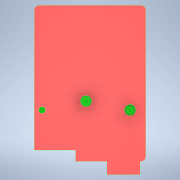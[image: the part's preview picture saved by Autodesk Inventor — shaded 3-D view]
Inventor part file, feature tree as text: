
AUTODESK INVENTOR PART (.ipt)
format: ipt  version: 2022 (Build 260153000, 153)  size: 168,448 bytes
history: native  units: mm
features: extrude x6, sketch x4, fillet x1
ambient origin geometry x8: Origin, YZ Plane, XZ Plane, XY Plane, X Axis, Y Axis, Z Axis, Center Point
bodies: Body1 (feature_tree)
feature tree (11):
  extrude  "Extrusion3"  Depth=70.0mm
  fillet  "Fillet1"  Radius=6.0mm
  sketch  "Sketch4"  dims[d14=2.0mm d16=18.5mm]
  extrude  "Extrusion5"  Depth=18.5mm
  extrude  "Extrusion6"  Depth=5.0mm
  extrude  "Extrusion7"  Depth=20.0mm TaperAngle=0.0deg
  extrude  "Extrusion8"  Depth=5.0mm
  extrude  "Extrusion9"  Depth=6.0mm
  sketch  "Sketch2"  dims[d0=50.0mm d1=70.0mm d12=6.0mm d13=0.0mm]
  sketch  "Sketch5"  dims[d17=5.0mm d31=5.0mm]
  sketch  "Sketch6"  dims[d34=3.0mm d37=20.0mm d38=0.0mm d41=5.0mm d44=19.75mm d45=19.75mm d46=7.0mm d48=5.6mm d49=0.0mm d50=3.0mm d51=14.5mm d52=0.0mm d53=10.64mm d54=0.0mm d55=3.0mm d56=9.36mm d57=0.0mm d58=2.5mm d59=15.0mm d60=6.0mm d61=23.0mm d62=27.0mm d63=23.0mm d4=0.0mm d5=0.0mm d6=0.0mm d7=0.0mm]
